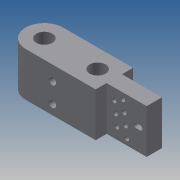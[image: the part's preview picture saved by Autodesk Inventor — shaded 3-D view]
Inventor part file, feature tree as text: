
AUTODESK INVENTOR PART (.ipt)
format: ipt  version: 2013 (Build 170138000, 138)  size: 182,784 bytes
history: native  units: mm
features: extrude x8, sketch x8
ambient origin geometry x8: Origin, YZ Plane, XZ Plane, XY Plane, X Axis, Y Axis, Z Axis, Center Point
bodies: Solid1 (feature_tree)
feature tree (16):
  extrude  "Extrusion1"  Depth=30.0mm
  extrude  "Extrusion2"  Depth=11.5mm
  extrude  "Extrusion3"  Depth=12.0mm
  extrude  "Extrusion4"  Depth=33.0mm TaperAngle=0.0deg
  extrude  "Extrusion5"  Depth=5.0mm
  extrude  "Extrusion6"  Depth=10.0mm TaperAngle=0.0deg
  extrude  "Extrusion7"  Depth=7.0mm
  extrude  "Extrusion8"  Depth=8.0mm
  sketch  "Sketch1"  dims[d0=82.5mm d1=30.0mm]
  sketch  "Sketch2"  dims[d2=14.0mm d3=11.5mm]
  sketch  "Sketch3"  dims[d4=33.0mm d5=0.0mm d6=12.0mm]
  sketch  "Sketch4"  dims[d8=40.0mm d9=33.0mm d10=0.0mm]
  sketch  "Sketch5"  dims[d11=3.0mm d13=5.0mm]
  sketch  "Sketch6"  dims[d14=1.75mm d15=10.0mm d16=0.0mm]
  sketch  "Sketch7"  dims[d17=5.0mm d18=7.0mm]
  sketch  "Sketch8"  dims[d19=3.5mm d20=8.0mm d21=0.5mm d22=1.0mm d23=1.5mm d24=2.0mm d25=2.5mm d26=3.0mm d27=10.0mm d28=0.0mm d32=18.1mm d34=7.375mm d35=5.5mm d36=10.0mm d37=0.0mm d38=8.0mm d39=5.0mm d40=0.0mm d41=8.0mm d42=5.0mm d43=0.0mm d44=3.0mm d46=5.0mm d47=0.0mm]
